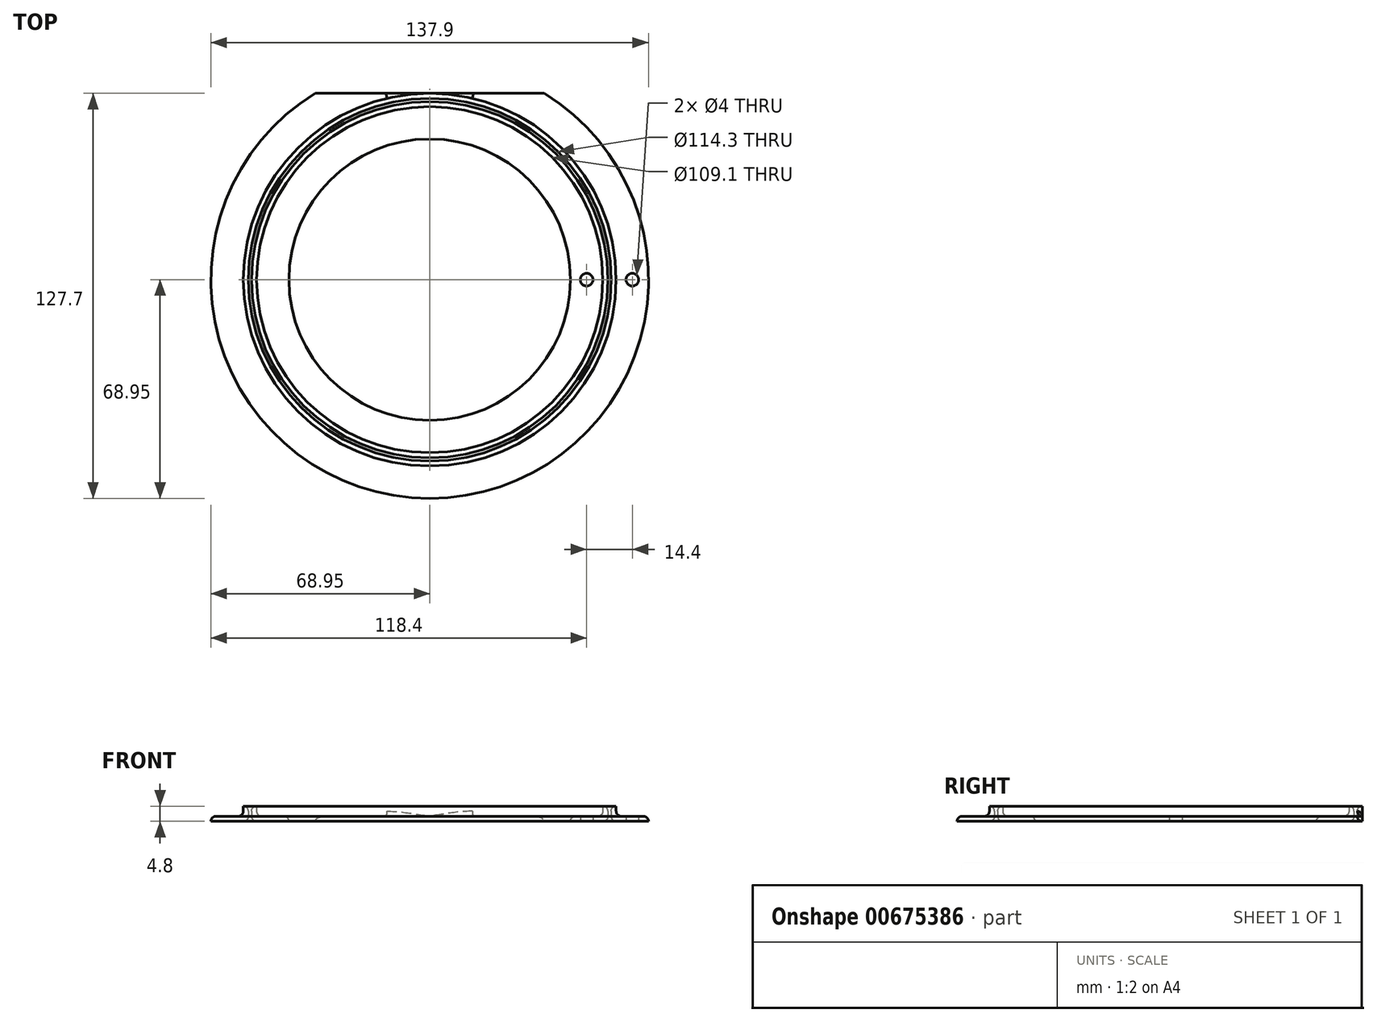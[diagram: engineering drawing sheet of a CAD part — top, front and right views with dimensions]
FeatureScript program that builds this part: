
annotation { "Feature Type Name" : "Feature", "Feature Type Description" : "" }
export const myFeature = defineFeature(function(context is Context, id is Id, definition is map)
    precondition{}
    {
        {
            assignVariable(context, id + "F0", {"name" : "Shells", "anyValue" : 2});
        }
        {
            assignVariable(context, id + "F1", {"name" : "Wall", "anyValue" : 0.4 * getVariable(context, 'Shells') * 2});
        }
        {
            assignVariable(context, id + "F2", {"name" : "Hole", "anyValue" : 4});
        }
        {
            var Q0;
            Q0=qCreatedBy(makeId("Front.planeOp"),FACE);
            var sketch = newSketch(context, id + "F3", { "sketchPlane" : qUnion([Q0])});
            skLineSegment(sketch, "E0", {"start": v(57.15, 0) * mm, "end": v(57.15, 4.8) * mm});
            skLineSegment(sketch, "E1", {"start": v(57.15, 4.8) * mm, "end": v(58.75, 4.8) * mm});
            skLineSegment(sketch, "E2", {"start": v(58.75, 4.8) * mm, "end": v(58.75, 0) * mm});
            skLineSegment(sketch, "E3", {"start": v(58.75, 0) * mm, "end": v(57.15, 0) * mm});
            skLineSegment(sketch, "E4", {"start": v(54.55, 4.8) * mm, "end": v(54.55, 0) * mm});
            skLineSegment(sketch, "E5", {"start": v(54.55, 0) * mm, "end": v(56.15, 0) * mm});
            skLineSegment(sketch, "E6", {"start": v(56.15, 0) * mm, "end": v(56.15, 4.8) * mm});
            skLineSegment(sketch, "E7", {"start": v(56.15, 4.8) * mm, "end": v(54.55, 4.8) * mm});
            skLineSegment(sketch, "E8", {"start": v(54.55, 0) * mm, "end": v(44.35, 0) * mm});
            skLineSegment(sketch, "E9", {"start": v(44.35, 0) * mm, "end": v(44.35, 1.6) * mm});
            skLineSegment(sketch, "E10", {"start": v(58.75, 0) * mm, "end": v(68.95, 0) * mm});
            skLineSegment(sketch, "E11", {"start": v(68.95, 0) * mm, "end": v(68.95, 1.6) * mm});
            skLineSegment(sketch, "E12", {"start": v(49.45, 0) * mm, "end": v(49.45, 1.6) * mm, "construction": true});
            skLineSegment(sketch, "E13", {"start": v(52.95, 0) * mm, "end": v(52.95, 1.6) * mm, "construction": true});
            skLineSegment(sketch, "E14.MirrorCS", {"start": v(45.95, 0) * mm, "end": v(45.95, 1.6) * mm, "construction": true});
            skLineSegment(sketch, "E15", {"start": v(44.35, 1.6) * mm, "end": v(54.55, 1.6) * mm});
            skLineSegment(sketch, "E16", {"start": v(68.95, 1.6) * mm, "end": v(58.75, 1.6) * mm});
            skLineSegment(sketch, "E17", {"start": v(0, 0) * mm, "end": v(0, 4.8) * mm});
            skSolve(sketch);
        }
        {
            var Q0;
            {var subQ0=sQuery(id+"F3.wireOp",EDGE,"E5");Q0=makeQuery(id+"F3.imprint","IMPRINT",FACE,{"disambiguationData":[TD([[makeQuery(id+"F3.imprint","IMPRINT",EDGE,{"derivedFrom":subQ0}),1.0]])]});}
            var Q1;
            Q1=makeQuery(id+"F3.imprint","IMPRINT",FACE,{"disambiguationData":[TD([[makeQuery(id+"F3.imprint","IMPRINT",EDGE,{"derivedFrom":sQuery(id+"F3.wireOp",EDGE,"E0")}),-1.0]])]});
            var Q2;
            {var subQ0=sQuery(id+"F3.wireOp",EDGE,"E10");Q2=makeQuery(id+"F3.imprint","IMPRINT",FACE,{"disambiguationData":[TD([[makeQuery(id+"F3.imprint","IMPRINT",EDGE,{"derivedFrom":subQ0}),1.0]])]});}
            var Q3;
            {var subQ0=sQuery(id+"F3.wireOp",EDGE,"E8");Q3=makeQuery(id+"F3.imprint","IMPRINT",FACE,{"disambiguationData":[TD([[makeQuery(id+"F3.imprint","IMPRINT",EDGE,{"derivedFrom":subQ0}),-1.0]])]});}
            var Q4;
            Q4=sQuery(id+"F3.wireOp",EDGE,"E17");
            revolve(context, id + "F4", {"entities" : qUnion([Q0, Q1, Q2, Q3]), "axis" : qUnion([Q4]), "revolveType" : RevolveType.FULL});
        }
        {
            var Q0;
            Q0=qCreatedBy(makeId("Top.planeOp"),FACE);
            var sketch = newSketch(context, id + "F5", { "sketchPlane" : qUnion([Q0])});
            skPoint(sketch, "E18.0", {"position": v(63.85, 0) * mm});
            skPoint(sketch, "E19.0", {"position": v(49.45, 0) * mm});
            skCircle(sketch, "E20", {"center": v(0, 0) * mm, "radius": 54.55 * mm, "construction": true});
            skCircle(sketch, "E21", {"center": v(0, 0) * mm, "radius": 58.75 * mm, "construction": true});
            skSolve(sketch);
        }
        {
            var Q0;
            Q0=qCreatedBy(makeId("Top.planeOp"),FACE);
            var sketch = newSketch(context, id + "F6", { "sketchPlane" : qUnion([Q0])});
            skLineSegment(sketch, "E22", {"start": v(-58.75, 58.75) * mm, "end": v(58.75, 58.75) * mm});
            skLineSegment(sketch, "E23", {"start": v(-58.75, 58.75) * mm, "end": v(-58.75, 0) * mm, "construction": true});
            skLineSegment(sketch, "E24", {"start": v(58.75, 58.75) * mm, "end": v(58.75, 0) * mm, "construction": true});
            skLineSegment(sketch, "E25", {"start": v(-58.75, 58.75) * mm, "end": v(-58.75, 83.88) * mm});
            skLineSegment(sketch, "E26", {"start": v(-58.75, 83.88) * mm, "end": v(58.75, 83.88) * mm});
            skLineSegment(sketch, "E27", {"start": v(58.75, 83.88) * mm, "end": v(58.75, 58.75) * mm});
            skSolve(sketch);
        }
        {
            var Q0;
            Q0=makeQuery(id+"F6.imprint","IMPRINT",FACE,{"disambiguationData":[TD([[makeQuery(id+"F6.imprint","IMPRINT",EDGE,{"derivedFrom":sQuery(id+"F6.wireOp",EDGE,"E22")}),1.0]])]});
            extrude(context, id + "F7", {"entities" : qUnion([Q0]), "operationType" : NewBodyOperationType.REMOVE, "depth" : 25 * mm, "offsetDistance" : 25 * mm});
        }
        {
            var Q0;
            Q0=makeQuery(id+"F4.opRevolve","SWEPT_EDGE",EDGE,{"disambiguationData":[OSD([sQuery(id+"F3.wireOp",EDGE,"E4"),sQuery(id+"F3.wireOp",EDGE,"E15")])]});
            var Q1;
            Q1=makeQuery(id+"F4.opRevolve","SWEPT_EDGE",EDGE,{"disambiguationData":[OSD([sQuery(id+"F3.wireOp",EDGE,"E2"),sQuery(id+"F3.wireOp",EDGE,"E16")])]});
            var Q2;
            Q2=makeQuery(id+"F4.opRevolve","SWEPT_EDGE",EDGE,{"disambiguationData":[OSD([sQuery(id+"F3.wireOp",EDGE,"E0"),sQuery(id+"F3.wireOp",EDGE,"E3")])]});
            var Q3;
            Q3=makeQuery(id+"F4.opRevolve","SWEPT_EDGE",EDGE,{"disambiguationData":[OSD([sQuery(id+"F3.wireOp",EDGE,"E5"),sQuery(id+"F3.wireOp",EDGE,"E6")])]});
            var Q4;
            Q4=makeQuery(id+"F4.opRevolve","SWEPT_EDGE",EDGE,{"disambiguationData":[OSD([sQuery(id+"F3.wireOp",EDGE,"E0"),sQuery(id+"F3.wireOp",EDGE,"E1")])]});
            var Q5;
            Q5=makeQuery(id+"F4.opRevolve","SWEPT_EDGE",EDGE,{"disambiguationData":[OSD([sQuery(id+"F3.wireOp",EDGE,"E6"),sQuery(id+"F3.wireOp",EDGE,"E7")])]});
            var Q6;
            Q6=makeQuery(id+"F4.opRevolve","SWEPT_EDGE",EDGE,{"disambiguationData":[OSD([sQuery(id+"F3.wireOp",EDGE,"E11"),sQuery(id+"F3.wireOp",EDGE,"E16")])]});
            var Q7;
            Q7=makeQuery(id+"F4.opRevolve","SWEPT_EDGE",EDGE,{"disambiguationData":[OSD([sQuery(id+"F3.wireOp",EDGE,"E9"),sQuery(id+"F3.wireOp",EDGE,"E15")])]});
            fillet(context, id + "F8", {"entities" : qUnion([Q0, Q1, Q2, Q3, Q4, Q5, Q6, Q7]), "radius" : (getVariable(context, 'Wall')) * mm, "tangentPropagation" : true, "allowEdgeOverflow" : false});
        }
        {
            var Q0;
            Q0=sQuery(id+"F5.wireOp",VERTEX,"E19.0");
            var Q1;
            Q1=sQuery(id+"F5.wireOp",VERTEX,"E18.0");
            var Q2;
            Q2=makeQuery(id+"F4.opRevolve","SWEPT_BODY",BODY,{"disambiguationData":[OSD([sQuery(id+"F3.wireOp",EDGE,"E4"),sQuery(id+"F3.wireOp",EDGE,"E5"),sQuery(id+"F3.wireOp",EDGE,"E6"),sQuery(id+"F3.wireOp",EDGE,"E7"),sQuery(id+"F3.wireOp",EDGE,"E8"),sQuery(id+"F3.wireOp",EDGE,"E9"),sQuery(id+"F3.wireOp",EDGE,"E15")])]});
            var Q3;
            Q3=makeQuery(id+"F4.opRevolve","SWEPT_BODY",BODY,{"disambiguationData":[OSD([sQuery(id+"F3.wireOp",EDGE,"E0"),sQuery(id+"F3.wireOp",EDGE,"E1"),sQuery(id+"F3.wireOp",EDGE,"E2"),sQuery(id+"F3.wireOp",EDGE,"E3"),sQuery(id+"F3.wireOp",EDGE,"E10"),sQuery(id+"F3.wireOp",EDGE,"E11"),sQuery(id+"F3.wireOp",EDGE,"E16")])]});
            hole(context, id + "F9", {"style" : HoleStyle.SIMPLE, "endStyle" : HoleEndStyle.THROUGH, "oppositeDirection" : true, "holeDiameter" : (getVariable(context, 'Hole')) * mm, "majorDiameter" : 5 * mm, "isTappedThrough" : true, "tappedDepth" : 12 * mm, "tapClearance" : 3, "locations" : qUnion([Q0, Q1]), "scope" : qUnion([Q2, Q3])});
        }
    });
